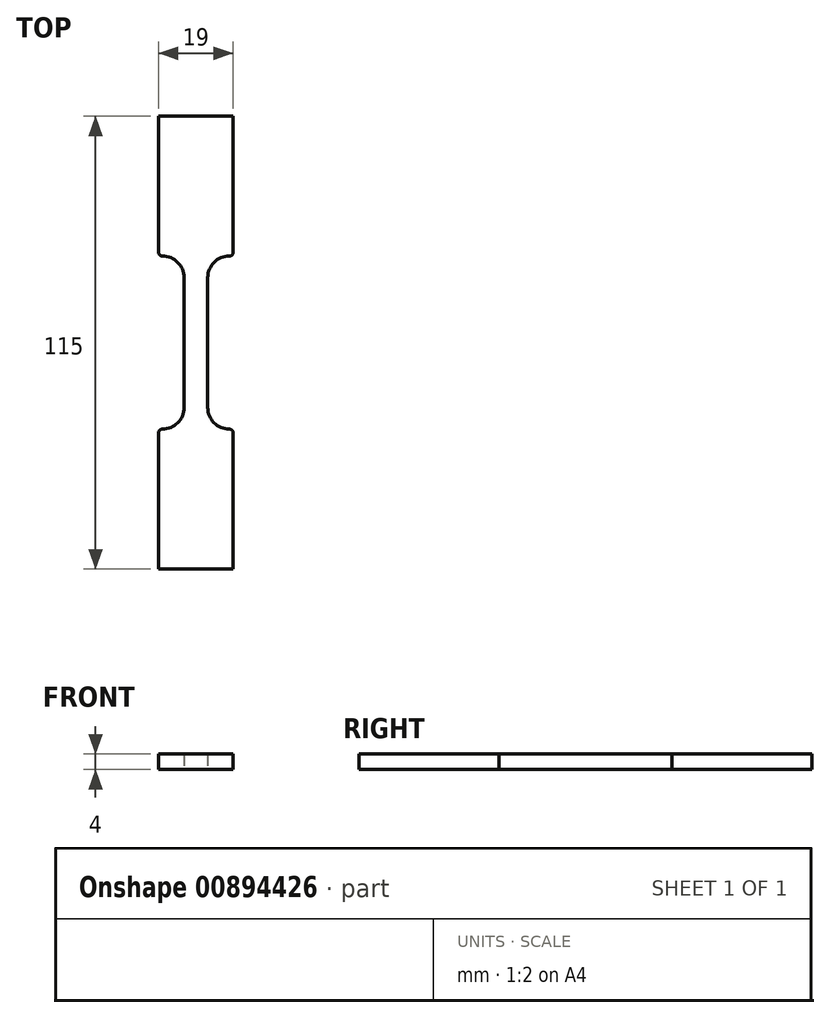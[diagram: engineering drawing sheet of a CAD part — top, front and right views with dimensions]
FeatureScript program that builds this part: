
annotation { "Feature Type Name" : "Feature", "Feature Type Description" : "" }
export const myFeature = defineFeature(function(context is Context, id is Id, definition is map)
    precondition{}
    {
        {
            var Q0;
            Q0=qCreatedBy(makeId("Top.planeOp"),FACE);
            var sketch = newSketch(context, id + "F0", { "sketchPlane" : qUnion([Q0])});
            skLineSegment(sketch, "E0", {"start": v(0, 57.5) * mm, "end": v(-9.5, 57.5) * mm});
            skLineSegment(sketch, "E1", {"start": v(-9.5, 57.5) * mm, "end": v(-9.5, 23) * mm});
            skLineSegment(sketch, "E2", {"start": v(-8.5, 22) * mm, "end": v(-8.5, 22) * mm});
            skLineSegment(sketch, "E3", {"start": v(-3, 16.5) * mm, "end": v(-3, 0) * mm});
            skLineSegment(sketch, "E4.MirrorCS", {"start": v(0, 57.5) * mm, "end": v(9.5, 57.5) * mm});
            skLineSegment(sketch, "E5.MirrorCS", {"start": v(9.5, 57.5) * mm, "end": v(9.5, 23) * mm});
            skLineSegment(sketch, "E6.MirrorCS", {"start": v(8.5, 22) * mm, "end": v(8.5, 22) * mm});
            skLineSegment(sketch, "E7.MirrorCS", {"start": v(3, 16.5) * mm, "end": v(3, 0) * mm});
            skLineSegment(sketch, "E8.MirrorCS", {"start": v(9.5, -57.5) * mm, "end": v(9.5, -23) * mm});
            skLineSegment(sketch, "E9.MirrorCS", {"start": v(3, -16.5) * mm, "end": v(3, 0) * mm});
            skLineSegment(sketch, "E10.MirrorCS", {"start": v(-9.5, -57.5) * mm, "end": v(-9.5, -23) * mm});
            skLineSegment(sketch, "E11.MirrorCS", {"start": v(-8.5, -22) * mm, "end": v(-8.5, -22) * mm});
            skLineSegment(sketch, "E12.MirrorCS", {"start": v(-3, -16.5) * mm, "end": v(-3, 0) * mm});
            skLineSegment(sketch, "E13.MirrorCS", {"start": v(0, -57.5) * mm, "end": v(-9.5, -57.5) * mm});
            skLineSegment(sketch, "E14.MirrorCS", {"start": v(0, -57.5) * mm, "end": v(9.5, -57.5) * mm});
            skLineSegment(sketch, "E15.MirrorCS", {"start": v(8.5, -22) * mm, "end": v(8.5, -22) * mm});
            skPoint(sketch, "E16.visualSharp", {"position": v(3, -22) * mm});
            skArc(sketch, "E16.filletArc", {"start": v(3, -16.5) * mm, "mid": v(4.61, -20.39) * mm, "end": v(8.5, -22) * mm});
            skPoint(sketch, "E17.visualSharp", {"position": v(9.5, -22) * mm});
            skArc(sketch, "E17.filletArc", {"start": v(9.5, -23) * mm, "mid": v(9.2, -22.3) * mm, "end": v(8.5, -22) * mm});
            skPoint(sketch, "E18.visualSharp", {"position": v(-3, -22) * mm});
            skArc(sketch, "E18.filletArc", {"start": v(-8.5, -22) * mm, "mid": v(-4.61, -20.39) * mm, "end": v(-3, -16.5) * mm});
            skPoint(sketch, "E19.visualSharp", {"position": v(-9.5, -22) * mm});
            skArc(sketch, "E19.filletArc", {"start": v(-8.5, -22) * mm, "mid": v(-9.2, -22.3) * mm, "end": v(-9.5, -23) * mm});
            skPoint(sketch, "E20.visualSharp", {"position": v(3, 22) * mm});
            skArc(sketch, "E20.filletArc", {"start": v(8.5, 22) * mm, "mid": v(4.61, 20.39) * mm, "end": v(3, 16.5) * mm});
            skPoint(sketch, "E21.visualSharp", {"position": v(-3, 22) * mm});
            skArc(sketch, "E21.filletArc", {"start": v(-3, 16.5) * mm, "mid": v(-4.61, 20.39) * mm, "end": v(-8.5, 22) * mm});
            skPoint(sketch, "E22.visualSharp", {"position": v(-9.5, 22) * mm});
            skArc(sketch, "E22.filletArc", {"start": v(-9.5, 23) * mm, "mid": v(-9.2, 22.3) * mm, "end": v(-8.5, 22) * mm});
            skPoint(sketch, "E23.visualSharp", {"position": v(9.5, 22) * mm});
            skArc(sketch, "E23.filletArc", {"start": v(8.5, 22) * mm, "mid": v(9.2, 22.3) * mm, "end": v(9.5, 23) * mm});
            skSolve(sketch);
        }
        {
            var Q0;
            Q0=makeQuery(id+"F0.imprint","IMPRINT",FACE,{"disambiguationData":[TD([[makeQuery(id+"F0.imprint","IMPRINT",EDGE,{"derivedFrom":sQuery(id+"F0.wireOp",EDGE,"E0")}),1.0]])]});
            extrude(context, id + "F1", {"entities" : qUnion([Q0]), "depth" : 4 * mm, "offsetDistance" : 25 * mm});
        }
    });
